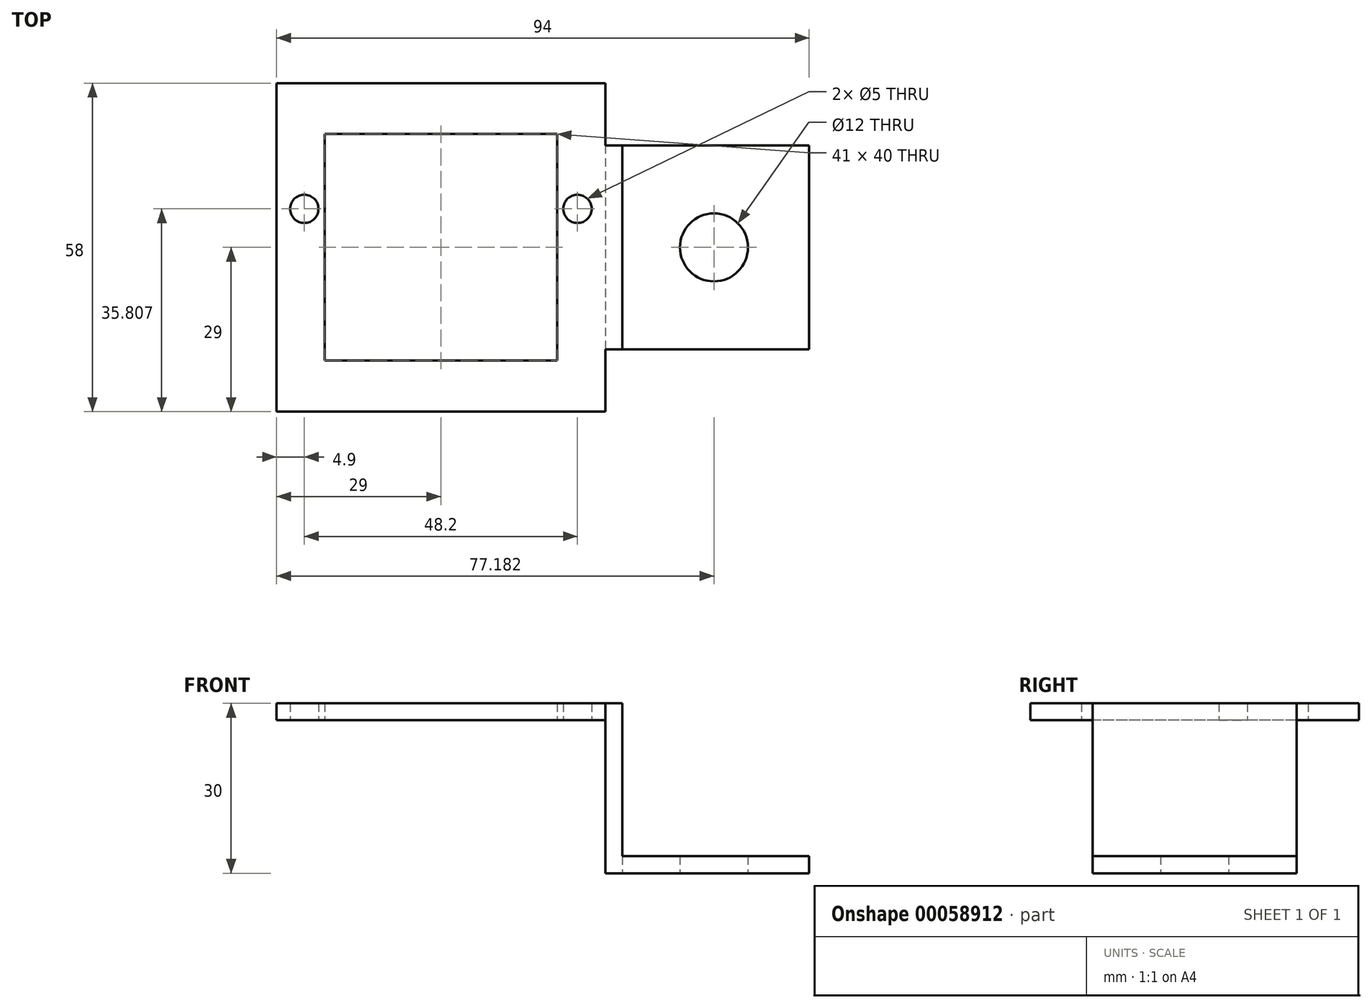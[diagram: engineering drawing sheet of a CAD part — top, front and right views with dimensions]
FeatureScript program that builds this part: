
annotation { "Feature Type Name" : "Feature", "Feature Type Description" : "" }
export const myFeature = defineFeature(function(context is Context, id is Id, definition is map)
    precondition{}
    {
        {
            var Q0;
            Q0=qCreatedBy(makeId("Top.planeOp"),FACE);
            var sketch = newSketch(context, id + "F0", { "sketchPlane" : qUnion([Q0])});
            skLineSegment(sketch, "E0.rect.bottom", {"start": v(29, 29) * mm, "end": v(-29, 29) * mm});
            skLineSegment(sketch, "E0.rect.top", {"start": v(29, -29) * mm, "end": v(-29, -29) * mm});
            skLineSegment(sketch, "E0.rect.left", {"start": v(29, 29) * mm, "end": v(29, -29) * mm});
            skLineSegment(sketch, "E0.rect.right", {"start": v(-29, 29) * mm, "end": v(-29, -29) * mm});
            skPoint(sketch, "E0.rect.middle", {"position": v(0, 0) * mm});
            skLineSegment(sketch, "E1.rect.bottom", {"start": v(20.5, 20) * mm, "end": v(-20.5, 20) * mm});
            skLineSegment(sketch, "E1.rect.top", {"start": v(20.5, -20) * mm, "end": v(-20.5, -20) * mm});
            skLineSegment(sketch, "E1.rect.left", {"start": v(20.5, 20) * mm, "end": v(20.5, -20) * mm});
            skLineSegment(sketch, "E1.rect.right", {"start": v(-20.5, 20) * mm, "end": v(-20.5, -20) * mm});
            skCircle(sketch, "E2", {"center": v(24.1, 6.8) * mm, "radius": 2.5 * mm});
            skCircle(sketch, "E3.MirrorC", {"center": v(-24.1, 6.8) * mm, "radius": 2.5 * mm});
            skSolve(sketch);
        }
        {
            var Q0;
            Q0=makeQuery(id+"F0.imprint","IMPRINT",FACE,{"disambiguationData":[TD([[makeQuery(id+"F0.imprint","IMPRINT",EDGE,{"derivedFrom":sQuery(id+"F0.wireOp",EDGE,"E0.rect.bottom")}),1.0]])]});
            extrude(context, id + "F1", {"entities" : qUnion([Q0]), "depth" : 3 * mm});
        }
        {
            var Q0;
            Q0=makeQuery(id+"F1.opExtrude","SWEPT_FACE",FACE,{"disambiguationData":[OSD([sQuery(id+"F0.wireOp",EDGE,"E0.rect.left")])]});
            var sketch = newSketch(context, id + "F2", { "sketchPlane" : qUnion([Q0])});
            skLineSegment(sketch, "E4.bottom", {"start": v(-17.98, 3) * mm, "end": v(18.02, 3) * mm});
            skLineSegment(sketch, "E4.top", {"start": v(-17.98, -27) * mm, "end": v(18.02, -27) * mm});
            skLineSegment(sketch, "E4.left", {"start": v(-17.98, 3) * mm, "end": v(-17.98, -27) * mm});
            skLineSegment(sketch, "E4.right", {"start": v(18.02, 3) * mm, "end": v(18.02, -27) * mm});
            skSolve(sketch);
        }
        {
            var Q0;
            {var subQ0=sQuery(id+"F2.wireOp",EDGE,"E4.top");Q0=makeQuery(id+"F2.imprint","IMPRINT",FACE,{"disambiguationData":[TD([[makeQuery(id+"F2.imprint","IMPRINT",EDGE,{"derivedFrom":subQ0}),1.0]])]});}
            var Q1;
            {var subQ0=sQuery(id+"F2.wireOp",EDGE,"E4.bottom");Q1=makeQuery(id+"F2.imprint","IMPRINT",FACE,{"disambiguationData":[TD([[makeQuery(id+"F2.imprint","IMPRINT",EDGE,{"derivedFrom":subQ0}),1.0]])]});}
            extrude(context, id + "F3", {"entities" : qUnion([Q0, Q1]), "operationType" : NewBodyOperationType.ADD, "depth" : 3 * mm});
        }
        {
            var Q0;
            Q0=makeQuery(id+"F3.opExtrude","SWEPT_FACE",FACE,{"disambiguationData":[OSD([sQuery(id+"F2.wireOp",EDGE,"E4.top")])]});
            var sketch = newSketch(context, id + "F4", { "sketchPlane" : qUnion([Q0])});
            skLineSegment(sketch, "E5.bottom", {"start": v(29, 17.98) * mm, "end": v(65, 17.98) * mm});
            skLineSegment(sketch, "E5.top", {"start": v(29, -18) * mm, "end": v(65, -18) * mm});
            skLineSegment(sketch, "E5.left", {"start": v(29, 17.98) * mm, "end": v(29, -18) * mm});
            skLineSegment(sketch, "E5.right", {"start": v(65, 17.98) * mm, "end": v(65, -18) * mm});
            skCircle(sketch, "E6", {"center": v(48.18, 0) * mm, "radius": 6 * mm});
            skSolve(sketch);
        }
        {
            var Q0;
            {var subQ0=sQuery(id+"F4.wireOp",EDGE,"E5.right");Q0=makeQuery(id+"F4.imprint","IMPRINT",FACE,{"disambiguationData":[TD([[makeQuery(id+"F4.imprint","IMPRINT",EDGE,{"derivedFrom":subQ0}),-1.0]])]});}
            extrude(context, id + "F5", {"entities" : qUnion([Q0]), "operationType" : NewBodyOperationType.ADD, "oppositeDirection" : true, "depth" : 3 * mm});
        }
    });
